# Revit family: Mop_Sink-Acorn-Terrazzo_Ware-TSH-36
name_source: partatom
category: Plumbing Fixtures
units: mm (PartAtom-declared; Revit-internal decimal feet)

## family parameters
Cut with Voids When Loaded = No
Host = Face
OmniClass Number = 23.45.05.14.14.27
OmniClass Title = Service Sinks
Part Type = Normal
Room Calculation Point = No
Round Connector Dimension = Use Diameter
Shared = Yes

## types (4) — shared parameters
Assembly Code = D2010440
BDS - Beehive Dome Strainer = No
CW Connection = No
CWFU = 3
Connection Size = 3"
Default Elevation = 0"
Drain Material = Metal-Acorn-Stainless Steel_Polished
HW Connection = No
HWFU = 3
Height = 12"
Installation Type = Floor Mounted
Integral Drain Diameter = 3"
KDG3 - Rubber Drain Gasket for 3" Waste Pipe = No
KDG32 Rubber Drain Gasket Reducer for 2" Waste Pipe = No
KF - Tiling Flange(s) (Shipped Loose) = No
KFC Chrome Utility Faucet, Hot & Cold, 8” Centerset (not Vandal Resistant; Shipped Loose) = No
KH36 - Hose 36" Long with Wall Hanger = No
KMH 3 Mop Hanger Stainless Steel Bracket = No
KWG Wall Guard (Shipped Loose) = No
LB - Lint Basket/Strainer = No
Manufacturer = Acorn Engineering Company
Material = Portland Cement-Acorn-Terazzo Marble Chips
Product Documentation Link = https://www.acorneng.com
Product Page URL = https://www.acorneng.com
SSC Stainless Steel Cap = No
Sink Material = Portland Cement-Acorn-Terazzo Marble Chips
TF1 Tiling Flange, Rear Side = Yes
TF2 Tiling Flange, Two Adjacent Sides  (Rear & Left Side) = No
TF2 Tiling Flange, Two Adjacent Sides  (Rear & Right Side) = No
TF3 Tiling Flange, Three Sides (Rear, Right and Left Sides) = No
Tiling Flange Material = Stainless Steel-Acorn-Galvanized
URL = http://www.acorneng.com
Vent Connection = No
WFU = 4
Waste Connection = Yes

## per-type parameters (varying)
| type | A Length | Description | Width |
| TSH-36-TF1 | 36" | 36" x 36" x 12" Standard Height Terrazzo Mop Sink | 36" |
| TSH-24-TF1 | 24" | 24" x 24" x 12" Standard Height Terrazzo Mop Sink | 24" |
| TSH-32-TF1 | 32" | 32" x 32" x 12" Standard Height Terrazzo Mop Sink | 32" |
| TSH-3624-TF1 | 36" | 36" x 24" x 12" Standard Height Terrazzo Mop Sink | 24" |

note: column(s) folded — value = type name in every type: Model

## geometry (parser evidence)
native form markers: Sweep x3
no freeform markers — native parametric forms only
